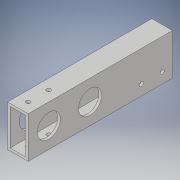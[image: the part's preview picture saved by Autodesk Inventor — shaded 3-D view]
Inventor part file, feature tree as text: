
AUTODESK INVENTOR PART (.ipt)
format: ipt  version: 2018 (Build 220112000, 112)  size: 153,600 bytes
history: native  units: in
note: dims shown in document units (in); Inventor stores cm internally (conversion verified against a paired STEP export)
features: extrude x2, hole x2, sketch x2, shell x1
ambient origin geometry x8: Origin, YZ Plane, XZ Plane, XY Plane, X Axis, Y Axis, Z Axis, Center Point
bodies: Solid1 (feature_tree)
feature tree (7):
  extrude  "Extrusion1"  Depth=7.0in
  shell  "Shell1"  Thickness=1.0in
  extrude  "Extrusion2"  Depth=1.0in
  hole  "Hole1"  [1 undecoded]
  hole  "Hole2"  [1 undecoded]
  sketch  "Sketch1"  dims[d0=2.0in d1=7.0in d2=1.0in d3=0.0in]
  sketch  "Sketch2"  dims[d4=0.125in d5=1.0in d6=1.125in d7=2.0in d8=1.125in d9=1.5in d10=1.5in d11=0.5in d12=0.5in d13=0.5in d14=0.5in d15=0.5in d16=0.5in d17=0.5in d18=0.5in d19=1.5in d20=1.5in d22=0.2031in d23=0.2031in d25=2.0in d26=0.0in d27=0.5in d28=0.5in d29=0.2031in d30=0.75in d31=0.375in d32=0.25in d33=0.5635in d34=1.0in d35=0.8108in d36=0.5in d37=1.5in d38=0.2031in d39=0.75in d40=0.375in d41=0.25in d42=0.5635in d43=1.0in d44=0.8108in]
note: 2 required parameter values undecoded (feature->parameter linkage not recoverable at this tier; creation-order binding heuristic only, values carry confidence <= 0.55)
